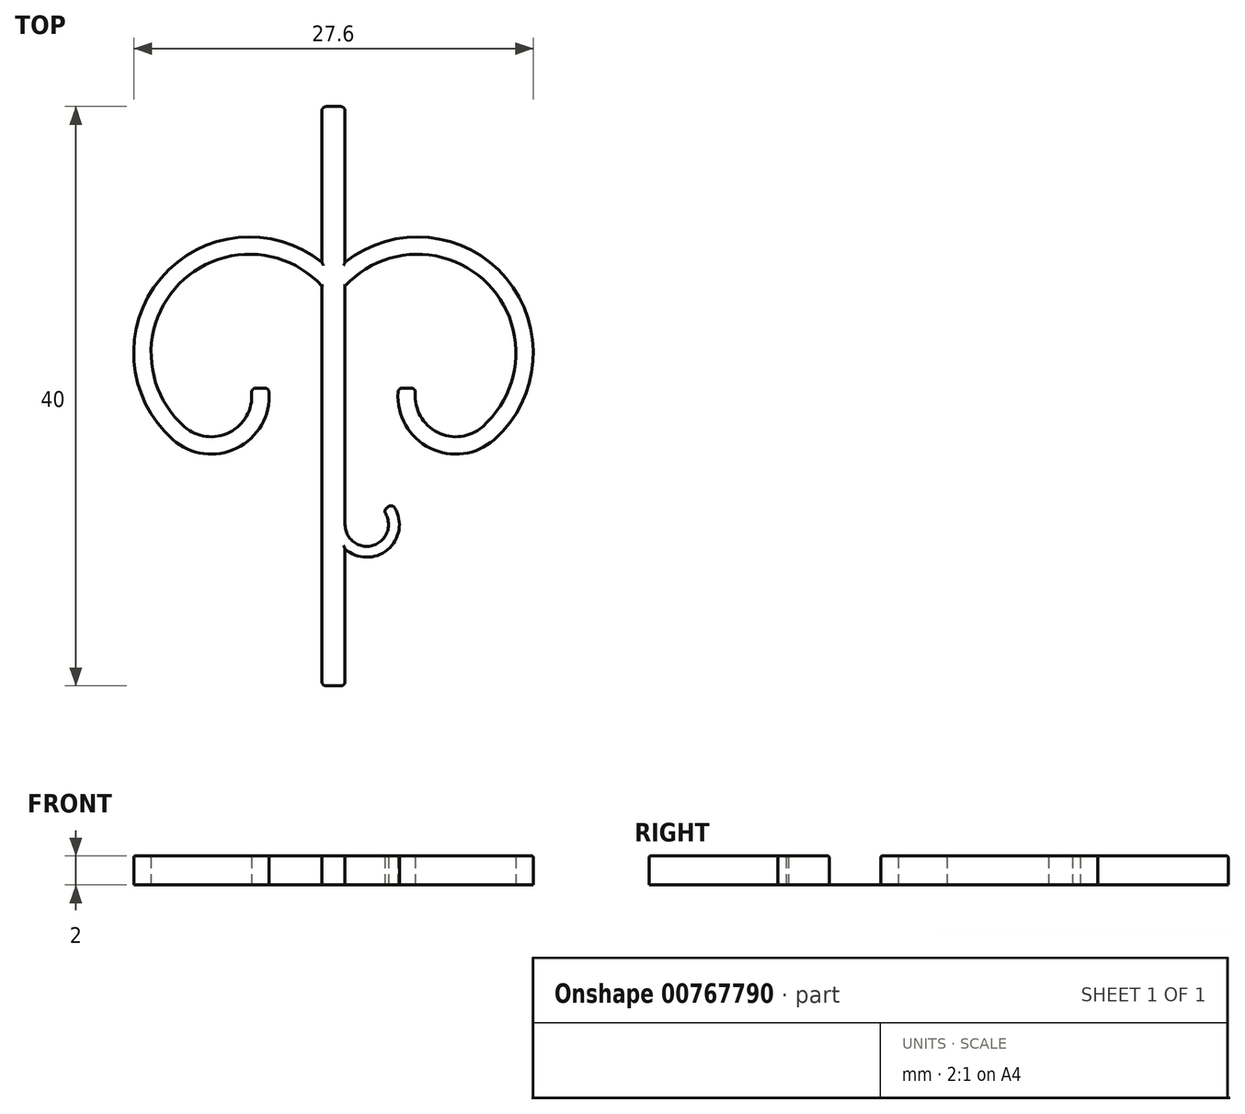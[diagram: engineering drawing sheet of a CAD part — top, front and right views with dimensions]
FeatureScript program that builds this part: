
annotation { "Feature Type Name" : "Feature", "Feature Type Description" : "" }
export const myFeature = defineFeature(function(context is Context, id is Id, definition is map)
    precondition{}
    {
        {
            var Q0;
            Q0=qCreatedBy(makeId("Top.planeOp"),FACE);
            var sketch = newSketch(context, id + "F0", { "sketchPlane" : qUnion([Q0])});
            skLineSegment(sketch, "E0.bottom", {"start": v(0, 0) * mm, "end": v(0.8, 0) * mm});
            skLineSegment(sketch, "E0.top", {"start": v(0, 40) * mm, "end": v(0.8, 40) * mm});
            skLineSegment(sketch, "E0.left", {"start": v(0, 0) * mm, "end": v(0, 40) * mm});
            skLineSegment(sketch, "E0.right", {"start": v(0.8, 0) * mm, "end": v(0.8, 27.6) * mm});
            skArc(sketch, "E1", {"start": v(11.1, 17) * mm, "mid": v(11.92, 28.15) * mm, "end": v(0.8, 29.24) * mm});
            skArc(sketch, "E2", {"start": v(10.3, 17.9) * mm, "mid": v(10.66, 27.76) * mm, "end": v(0.8, 27.6) * mm});
            skArc(sketch, "E3", {"start": v(4.49, 20.56) * mm, "mid": v(6.55, 16.48) * mm, "end": v(11.1, 17) * mm});
            skArc(sketch, "E4", {"start": v(5.7, 20.56) * mm, "mid": v(7.04, 17.58) * mm, "end": v(10.3, 17.9) * mm});
            skLineSegment(sketch, "E5", {"start": v(5.7, 20.56) * mm, "end": v(4.49, 20.56) * mm});
            skLineSegment(sketch, "E6.trimOffspring", {"start": v(0.8, 29.24) * mm, "end": v(0.8, 40) * mm});
            skLineSegment(sketch, "E7.MirrorCS", {"start": v(0, 40) * mm, "end": v(-0.8, 40) * mm});
            skLineSegment(sketch, "E8.MirrorCS", {"start": v(-0.8, 29.24) * mm, "end": v(-0.8, 40) * mm});
            skArc(sketch, "E9.MirrorCS", {"start": v(-11.1, 17) * mm, "mid": v(-11.92, 28.15) * mm, "end": v(-0.8, 29.24) * mm});
            skArc(sketch, "E10.MirrorCS", {"start": v(-10.3, 17.9) * mm, "mid": v(-10.66, 27.76) * mm, "end": v(-0.8, 27.6) * mm});
            skArc(sketch, "E11.MirrorCS", {"start": v(-5.7, 20.56) * mm, "mid": v(-7.04, 17.58) * mm, "end": v(-10.3, 17.9) * mm});
            skLineSegment(sketch, "E12.MirrorCS", {"start": v(-5.7, 20.56) * mm, "end": v(-4.49, 20.56) * mm});
            skArc(sketch, "E13.MirrorCS", {"start": v(-4.49, 20.56) * mm, "mid": v(-6.55, 16.48) * mm, "end": v(-11.1, 17) * mm});
            skLineSegment(sketch, "E14.MirrorCS", {"start": v(-0.8, 0) * mm, "end": v(-0.8, 27.6) * mm});
            skLineSegment(sketch, "E15.MirrorCS", {"start": v(0, 0) * mm, "end": v(-0.8, 0) * mm});
            skArc(sketch, "E16", {"start": v(0.8, 9.46) * mm, "mid": v(3.86, 9.52) * mm, "end": v(4.03, 12.58) * mm});
            skArc(sketch, "E17", {"start": v(0.8, 11.13) * mm, "mid": v(2.81, 9.72) * mm, "end": v(3.45, 12.1) * mm});
            skLineSegment(sketch, "E18", {"start": v(3.45, 12.1) * mm, "end": v(4.03, 12.58) * mm});
            skArc(sketch, "E19.MirrorCS", {"start": v(-0.8, 11.13) * mm, "mid": v(-2.81, 9.72) * mm, "end": v(-3.45, 12.1) * mm});
            skArc(sketch, "E20.MirrorCS", {"start": v(-0.8, 9.46) * mm, "mid": v(-3.86, 9.52) * mm, "end": v(-4.03, 12.58) * mm});
            skLineSegment(sketch, "E21.MirrorCS", {"start": v(-3.45, 12.1) * mm, "end": v(-4.03, 12.58) * mm});
            skSolve(sketch);
        }
        {
            var Q0;
            Q0=makeQuery(id+"F0.imprint","IMPRINT",FACE,{"disambiguationData":[TD([[makeQuery(id+"F0.imprint","IMPRINT",EDGE,{"derivedFrom":sQuery(id+"F0.wireOp",EDGE,"E0.bottom")}),1.0]])]});
            var Q1;
            Q1=makeQuery(id+"F0.imprint","IMPRINT",FACE,{"disambiguationData":[TD([[makeQuery(id+"F0.imprint","IMPRINT",EDGE,{"derivedFrom":sQuery(id+"F0.wireOp",EDGE,"E0.left")}),1.0]])]});
            var Q2;
            {var subQ0=sQuery(id+"F0.wireOp",EDGE,"E16");Q2=makeQuery(id+"F0.imprint","IMPRINT",FACE,{"disambiguationData":[TD([[makeQuery(id+"F0.imprint","IMPRINT",EDGE,{"derivedFrom":subQ0}),1.0]])]});}
            var Q3;
            {var subQ0=sQuery(id+"F0.wireOp",EDGE,"E19.MirrorCS");Q3=makeQuery(id+"F0.imprint","IMPRINT",FACE,{"disambiguationData":[TD([[makeQuery(id+"F0.imprint","IMPRINT",EDGE,{"derivedFrom":subQ0}),1.0]])]});}
            extrude(context, id + "F1", {"entities" : qUnion([Q0, Q1, Q2, Q3]), "depth" : 2 * mm, "offsetDistance" : 25 * mm});
        }
        {
            var Q0;
            Q0=makeQuery(id+"F1.opExtrude","CAP_FACE",FACE,{"disambiguationData":[OSD([sQuery(id+"F0.wireOp",EDGE,"E0.bottom"),sQuery(id+"F0.wireOp",EDGE,"E0.top"),sQuery(id+"F0.wireOp",EDGE,"E0.right"),sQuery(id+"F0.wireOp",EDGE,"E1"),sQuery(id+"F0.wireOp",EDGE,"E2"),sQuery(id+"F0.wireOp",EDGE,"E3"),sQuery(id+"F0.wireOp",EDGE,"E4"),sQuery(id+"F0.wireOp",EDGE,"E5"),sQuery(id+"F0.wireOp",EDGE,"E6.trimOffspring"),sQuery(id+"F0.wireOp",EDGE,"E7.MirrorCS"),sQuery(id+"F0.wireOp",EDGE,"E8.MirrorCS"),sQuery(id+"F0.wireOp",EDGE,"E9.MirrorCS"),sQuery(id+"F0.wireOp",EDGE,"E10.MirrorCS"),sQuery(id+"F0.wireOp",EDGE,"E11.MirrorCS"),sQuery(id+"F0.wireOp",EDGE,"E12.MirrorCS"),sQuery(id+"F0.wireOp",EDGE,"E13.MirrorCS"),sQuery(id+"F0.wireOp",EDGE,"E14.MirrorCS"),sQuery(id+"F0.wireOp",EDGE,"E15.MirrorCS"),sQuery(id+"F0.wireOp",EDGE,"E16"),sQuery(id+"F0.wireOp",EDGE,"E17"),sQuery(id+"F0.wireOp",EDGE,"E18"),sQuery(id+"F0.wireOp",EDGE,"E19.MirrorCS"),sQuery(id+"F0.wireOp",EDGE,"E20.MirrorCS"),sQuery(id+"F0.wireOp",EDGE,"E21.MirrorCS")])],"isStart":false});
            fillet(context, id + "F2", {"entities" : qUnion([Q0]), "radius" : 0.1 * mm, "tangentPropagation" : true, "allowEdgeOverflow" : false});
        }
        {
            var Q0;
            Q0=makeQuery(id+"F1.opExtrude","SWEPT_EDGE",EDGE,{"disambiguationData":[OSD([sQuery(id+"F0.wireOp",EDGE,"E16"),sQuery(id+"F0.wireOp",EDGE,"E18")])]});
            var Q1;
            Q1=makeQuery(id+"F1.opExtrude","SWEPT_EDGE",EDGE,{"disambiguationData":[OSD([sQuery(id+"F0.wireOp",EDGE,"E17"),sQuery(id+"F0.wireOp",EDGE,"E18")])]});
            var Q2;
            Q2=makeQuery(id+"F1.opExtrude","SWEPT_EDGE",EDGE,{"disambiguationData":[OSD([sQuery(id+"F0.wireOp",EDGE,"E20.MirrorCS"),sQuery(id+"F0.wireOp",EDGE,"E21.MirrorCS")])]});
            var Q3;
            Q3=makeQuery(id+"F1.opExtrude","SWEPT_EDGE",EDGE,{"disambiguationData":[OSD([sQuery(id+"F0.wireOp",EDGE,"E19.MirrorCS"),sQuery(id+"F0.wireOp",EDGE,"E21.MirrorCS")])]});
            var Q4;
            Q4=makeQuery(id+"F1.opExtrude","SWEPT_EDGE",EDGE,{"disambiguationData":[OSD([sQuery(id+"F0.wireOp",EDGE,"E4"),sQuery(id+"F0.wireOp",EDGE,"E5")])]});
            var Q5;
            Q5=makeQuery(id+"F1.opExtrude","SWEPT_EDGE",EDGE,{"disambiguationData":[OSD([sQuery(id+"F0.wireOp",EDGE,"E3"),sQuery(id+"F0.wireOp",EDGE,"E5")])]});
            var Q6;
            Q6=makeQuery(id+"F1.opExtrude","SWEPT_EDGE",EDGE,{"disambiguationData":[OSD([sQuery(id+"F0.wireOp",EDGE,"E12.MirrorCS"),sQuery(id+"F0.wireOp",EDGE,"E13.MirrorCS")])]});
            var Q7;
            Q7=makeQuery(id+"F1.opExtrude","SWEPT_EDGE",EDGE,{"disambiguationData":[OSD([sQuery(id+"F0.wireOp",EDGE,"E11.MirrorCS"),sQuery(id+"F0.wireOp",EDGE,"E12.MirrorCS")])]});
            var Q8;
            Q8=makeQuery(id+"F1.opExtrude","SWEPT_EDGE",EDGE,{"disambiguationData":[OSD([sQuery(id+"F0.wireOp",EDGE,"E7.MirrorCS"),sQuery(id+"F0.wireOp",EDGE,"E8.MirrorCS")])]});
            var Q9;
            Q9=makeQuery(id+"F1.opExtrude","SWEPT_EDGE",EDGE,{"disambiguationData":[OSD([sQuery(id+"F0.wireOp",EDGE,"E0.top"),sQuery(id+"F0.wireOp",EDGE,"E6.trimOffspring")])]});
            var Q10;
            Q10=makeQuery(id+"F1.opExtrude","SWEPT_EDGE",EDGE,{"disambiguationData":[OSD([sQuery(id+"F0.wireOp",EDGE,"E14.MirrorCS"),sQuery(id+"F0.wireOp",EDGE,"E15.MirrorCS")])]});
            var Q11;
            Q11=makeQuery(id+"F1.opExtrude","SWEPT_EDGE",EDGE,{"disambiguationData":[OSD([sQuery(id+"F0.wireOp",EDGE,"E0.bottom"),sQuery(id+"F0.wireOp",EDGE,"E0.right")])]});
            fillet(context, id + "F3", {"entities" : qUnion([Q0, Q1, Q2, Q3, Q4, Q5, Q6, Q7, Q8, Q9, Q10, Q11]), "radius" : 0.3 * mm, "tangentPropagation" : true, "allowEdgeOverflow" : false});
        }
    });
